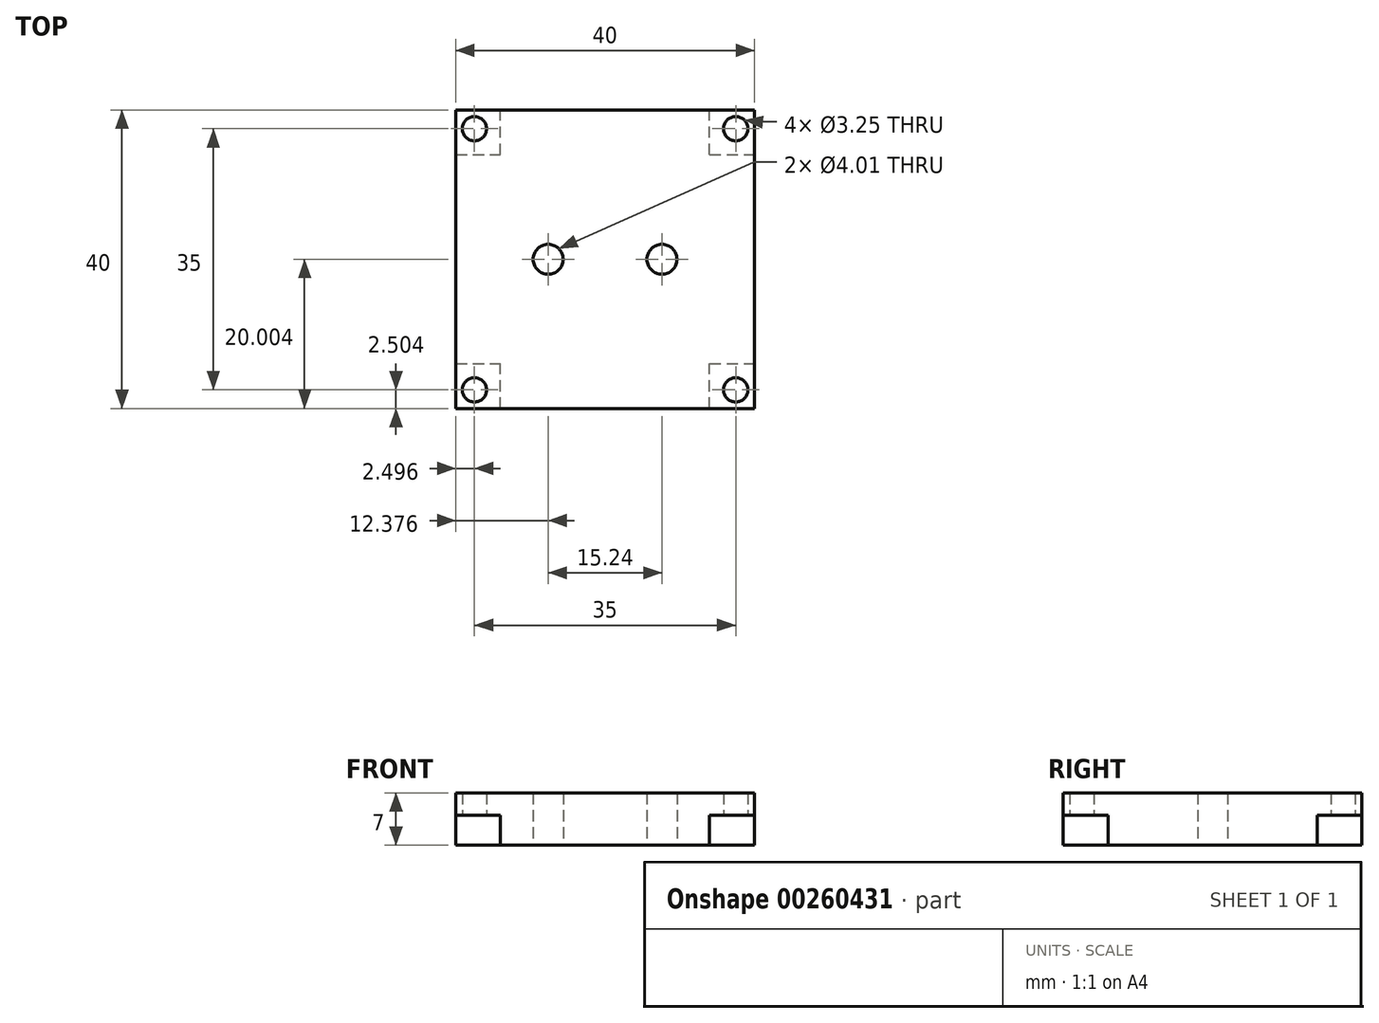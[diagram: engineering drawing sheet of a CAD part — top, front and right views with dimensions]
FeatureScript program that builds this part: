
annotation { "Feature Type Name" : "Feature", "Feature Type Description" : "" }
export const myFeature = defineFeature(function(context is Context, id is Id, definition is map)
    precondition{}
    {
        {
            var Q0;
            Q0=qCreatedBy(makeId("Top.planeOp"),FACE);
            var sketch = newSketch(context, id + "F0", { "sketchPlane" : qUnion([Q0])});
            skLineSegment(sketch, "E0.bottom", {"start": v(-42.54, -40.02) * mm, "end": v(-2.54, -40.02) * mm});
            skLineSegment(sketch, "E0.top", {"start": v(-42.54, -0.02) * mm, "end": v(-2.54, -0.02) * mm});
            skLineSegment(sketch, "E0.left", {"start": v(-42.54, -40.02) * mm, "end": v(-42.54, -0.02) * mm});
            skLineSegment(sketch, "E0.right", {"start": v(-2.54, -40.02) * mm, "end": v(-2.54, -0.02) * mm});
            skCircle(sketch, "E1", {"center": v(-40.04, -2.52) * mm, "radius": 1.63 * mm});
            skCircle(sketch, "E2.0.1.0", {"center": v(-40.04, -37.52) * mm, "radius": 1.63 * mm});
            skCircle(sketch, "E2.1.0.0", {"center": v(-5.04, -2.52) * mm, "radius": 1.63 * mm});
            skCircle(sketch, "E2.1.1.0", {"center": v(-5.04, -37.52) * mm, "radius": 1.63 * mm});
            skLineSegment(sketch, "E2.direction1", {"start": v(-40.04, -2.52) * mm, "end": v(-5.04, -2.52) * mm, "construction": true});
            skLineSegment(sketch, "E2.direction2", {"start": v(-40.04, -2.52) * mm, "end": v(-40.04, -37.52) * mm, "construction": true});
            skLineSegment(sketch, "E3", {"start": v(-22.54, -0.02) * mm, "end": v(-22.54, -40.02) * mm, "construction": true});
            skLineSegment(sketch, "E4", {"start": v(-2.54, -20.02) * mm, "end": v(-42.54, -20.02) * mm, "construction": true});
            skCircle(sketch, "E5", {"center": v(-30.16, -20.02) * mm, "radius": 2 * mm});
            skCircle(sketch, "E6.1.0.0", {"center": v(-14.92, -20.02) * mm, "radius": 2 * mm});
            skLineSegment(sketch, "E6.direction1", {"start": v(-30.16, -20.02) * mm, "end": v(-14.92, -20.02) * mm, "construction": true});
            skSolve(sketch);
        }
        {
            var Q0;
            Q0=makeQuery(id+"F0.imprint","IMPRINT",FACE,{"disambiguationData":[TD([[makeQuery(id+"F0.imprint","IMPRINT",EDGE,{"derivedFrom":sQuery(id+"F0.wireOp",EDGE,"E0.bottom")}),1.0]])]});
            extrude(context, id + "F1", {"entities" : qUnion([Q0]), "depth" : 7 * mm});
        }
        {
            var Q0;
            Q0=makeQuery(id+"F1.opExtrude","CAP_FACE",FACE,{"disambiguationData":[OSD([sQuery(id+"F0.wireOp",EDGE,"E0.bottom"),sQuery(id+"F0.wireOp",EDGE,"E0.top"),sQuery(id+"F0.wireOp",EDGE,"E0.left"),sQuery(id+"F0.wireOp",EDGE,"E0.right"),sQuery(id+"F0.wireOp",EDGE,"E1"),sQuery(id+"F0.wireOp",EDGE,"E2.0.1.0"),sQuery(id+"F0.wireOp",EDGE,"E2.1.0.0"),sQuery(id+"F0.wireOp",EDGE,"E2.1.1.0"),sQuery(id+"F0.wireOp",EDGE,"E5"),sQuery(id+"F0.wireOp",EDGE,"E6.1.0.0")])],"isStart":true});
            var sketch = newSketch(context, id + "F2", { "sketchPlane" : qUnion([Q0])});
            skLineSegment(sketch, "E7.bottom", {"start": v(-42.54, 40.02) * mm, "end": v(-36.54, 40.02) * mm});
            skLineSegment(sketch, "E7.top", {"start": v(-42.54, 34.02) * mm, "end": v(-36.54, 34.02) * mm});
            skLineSegment(sketch, "E7.left", {"start": v(-42.54, 40.02) * mm, "end": v(-42.54, 34.02) * mm});
            skLineSegment(sketch, "E7.right", {"start": v(-36.54, 40.02) * mm, "end": v(-36.54, 34.02) * mm});
            skLineSegment(sketch, "E8.0.1.0", {"start": v(-36.54, 6.02) * mm, "end": v(-36.54, 0.02) * mm});
            skLineSegment(sketch, "E8.0.1.1", {"start": v(-42.54, 6.02) * mm, "end": v(-42.54, 0.02) * mm});
            skLineSegment(sketch, "E8.0.1.2", {"start": v(-42.54, 0.02) * mm, "end": v(-36.54, 0.02) * mm});
            skLineSegment(sketch, "E8.0.1.3", {"start": v(-42.54, 6.02) * mm, "end": v(-36.54, 6.02) * mm});
            skLineSegment(sketch, "E8.1.0.0", {"start": v(-2.54, 40.02) * mm, "end": v(-2.54, 34.02) * mm});
            skLineSegment(sketch, "E8.1.0.1", {"start": v(-8.54, 40.02) * mm, "end": v(-8.54, 34.02) * mm});
            skLineSegment(sketch, "E8.1.0.2", {"start": v(-8.54, 34.02) * mm, "end": v(-2.54, 34.02) * mm});
            skLineSegment(sketch, "E8.1.0.3", {"start": v(-8.54, 40.02) * mm, "end": v(-2.54, 40.02) * mm});
            skLineSegment(sketch, "E8.1.1.0", {"start": v(-2.54, 6.02) * mm, "end": v(-2.54, 0.02) * mm});
            skLineSegment(sketch, "E8.1.1.1", {"start": v(-8.54, 6.02) * mm, "end": v(-8.54, 0.02) * mm});
            skLineSegment(sketch, "E8.1.1.2", {"start": v(-8.54, 0.02) * mm, "end": v(-2.54, 0.02) * mm});
            skLineSegment(sketch, "E8.1.1.3", {"start": v(-8.54, 6.02) * mm, "end": v(-2.54, 6.02) * mm});
            skLineSegment(sketch, "E8.direction1", {"start": v(-42.54, 34.02) * mm, "end": v(-8.54, 34.02) * mm, "construction": true});
            skLineSegment(sketch, "E8.direction2", {"start": v(-42.54, 34.02) * mm, "end": v(-42.54, 0.02) * mm, "construction": true});
            skSolve(sketch);
        }
        {
            var Q0;
            Q0=makeQuery(id+"F2.imprint","IMPRINT",FACE,{"disambiguationData":[TD([[makeQuery(id+"F2.imprint","IMPRINT",EDGE,{"derivedFrom":sQuery(id+"F2.wireOp",EDGE,"E7.bottom")}),-1.0]])]});
            var Q1;
            Q1=makeQuery(id+"F2.imprint","IMPRINT",FACE,{"disambiguationData":[TD([[makeQuery(id+"F2.imprint","IMPRINT",EDGE,{"derivedFrom":sQuery(id+"F2.wireOp",EDGE,"E8.1.0.0")}),-1.0]])]});
            var Q2;
            Q2=makeQuery(id+"F2.imprint","IMPRINT",FACE,{"disambiguationData":[TD([[makeQuery(id+"F2.imprint","IMPRINT",EDGE,{"derivedFrom":sQuery(id+"F2.wireOp",EDGE,"E8.1.1.0")}),-1.0]])]});
            var Q3;
            Q3=makeQuery(id+"F2.imprint","IMPRINT",FACE,{"disambiguationData":[TD([[makeQuery(id+"F2.imprint","IMPRINT",EDGE,{"derivedFrom":sQuery(id+"F2.wireOp",EDGE,"E8.0.1.0")}),-1.0]])]});
            extrude(context, id + "F3", {"entities" : qUnion([Q0, Q1, Q2, Q3]), "operationType" : NewBodyOperationType.REMOVE, "oppositeDirection" : true, "depth" : 4 * mm});
        }
    });
